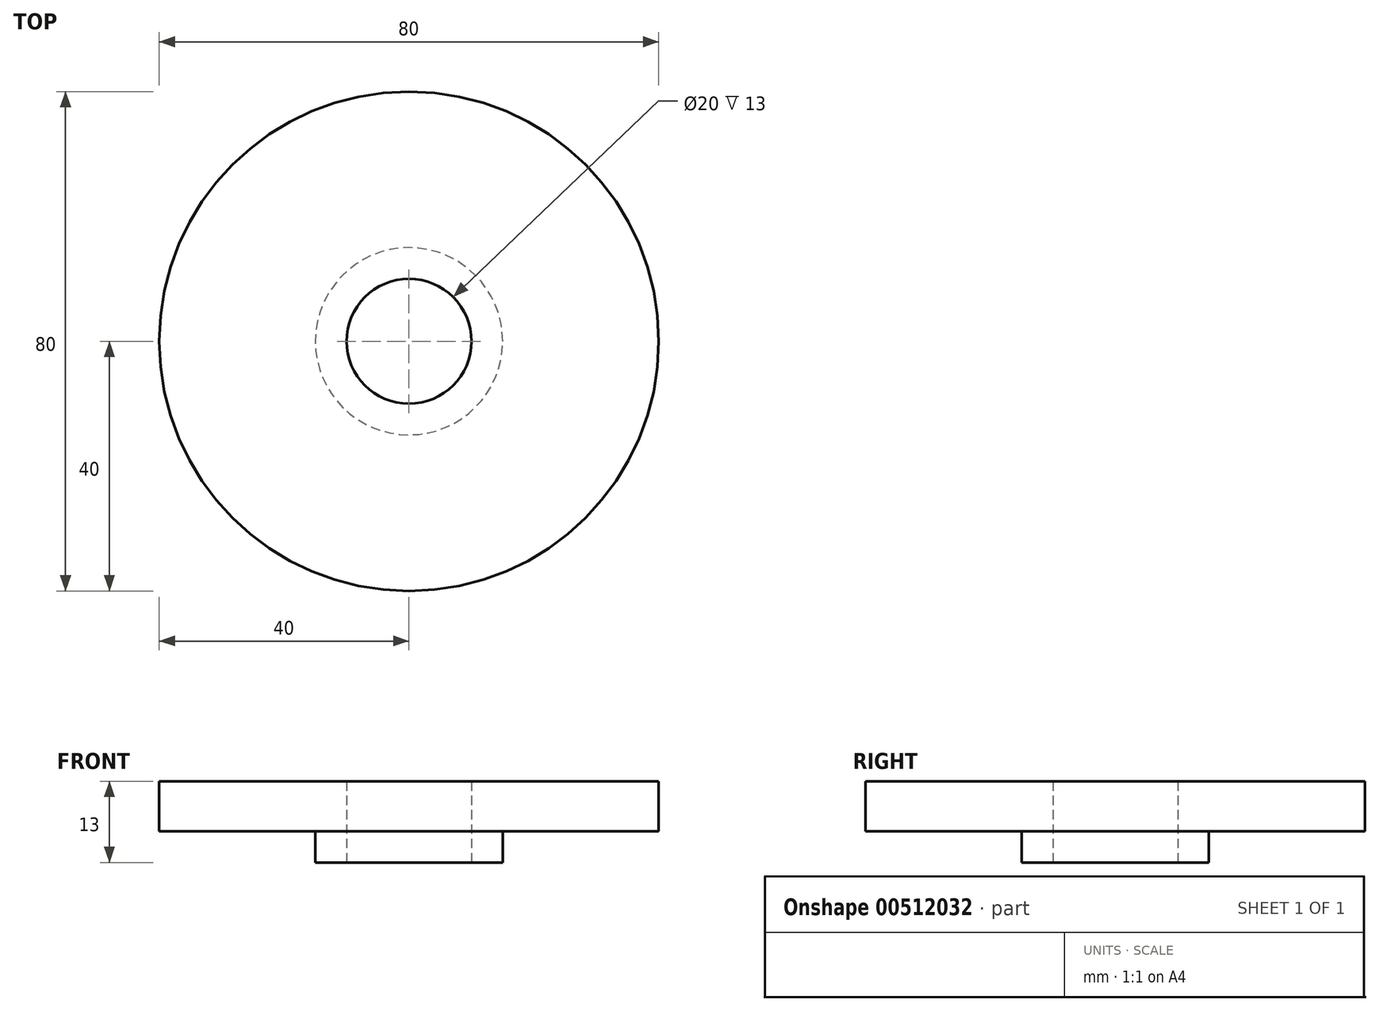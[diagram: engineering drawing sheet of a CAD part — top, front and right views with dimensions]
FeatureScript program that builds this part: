
annotation { "Feature Type Name" : "Feature", "Feature Type Description" : "" }
export const myFeature = defineFeature(function(context is Context, id is Id, definition is map)
    precondition{}
    {
        {
            var Q0;
            Q0=qCreatedBy(makeId("Top.planeOp"),FACE);
            var sketch = newSketch(context, id + "F0", { "sketchPlane" : qUnion([Q0])});
            skCircle(sketch, "E0", {"center": v(0, 0) * mm, "radius": 40 * mm});
            skCircle(sketch, "E1", {"center": v(0, 0) * mm, "radius": 15 * mm});
            skCircle(sketch, "E2", {"center": v(0, 0) * mm, "radius": 10 * mm});
            skSolve(sketch);
        }
        {
            var Q0;
            Q0 = qSketchRegion(id + "F0", true);
            var Q1;
            Q1=makeQuery(id+"F0.imprint","IMPRINT",FACE,{"disambiguationData":[TD([[makeQuery(id+"F0.imprint","IMPRINT",EDGE,{"derivedFrom":sQuery(id+"F0.wireOp",EDGE,"E1")}),1.0]])]});
            extrude(context, id + "F1", {"entities" : qUnion([Q0, Q1]), "depth" : 8 * mm});
        }
        {
            var Q0;
            Q0=makeQuery(id+"F0.imprint","IMPRINT",FACE,{"disambiguationData":[TD([[makeQuery(id+"F0.imprint","IMPRINT",EDGE,{"derivedFrom":sQuery(id+"F0.wireOp",EDGE,"E1")}),1.0]])]});
            extrude(context, id + "F2", {"entities" : qUnion([Q0]), "operationType" : NewBodyOperationType.ADD, "oppositeDirection" : true, "depth" : 5 * mm});
        }
        {
            var Q0;
            Q0=makeQuery(id+"F0.imprint","IMPRINT",FACE,{"disambiguationData":[TD([[makeQuery(id+"F0.imprint","IMPRINT",EDGE,{"derivedFrom":sQuery(id+"F0.wireOp",EDGE,"E2")}),1.0]])]});
            extrude(context, id + "F3", {"entities" : qUnion([Q0]), "operationType" : NewBodyOperationType.REMOVE, "endBound" : BoundingType.THROUGH_ALL, "oppositeDirection" : true, "depth" : 25 * mm});
        }
    });
